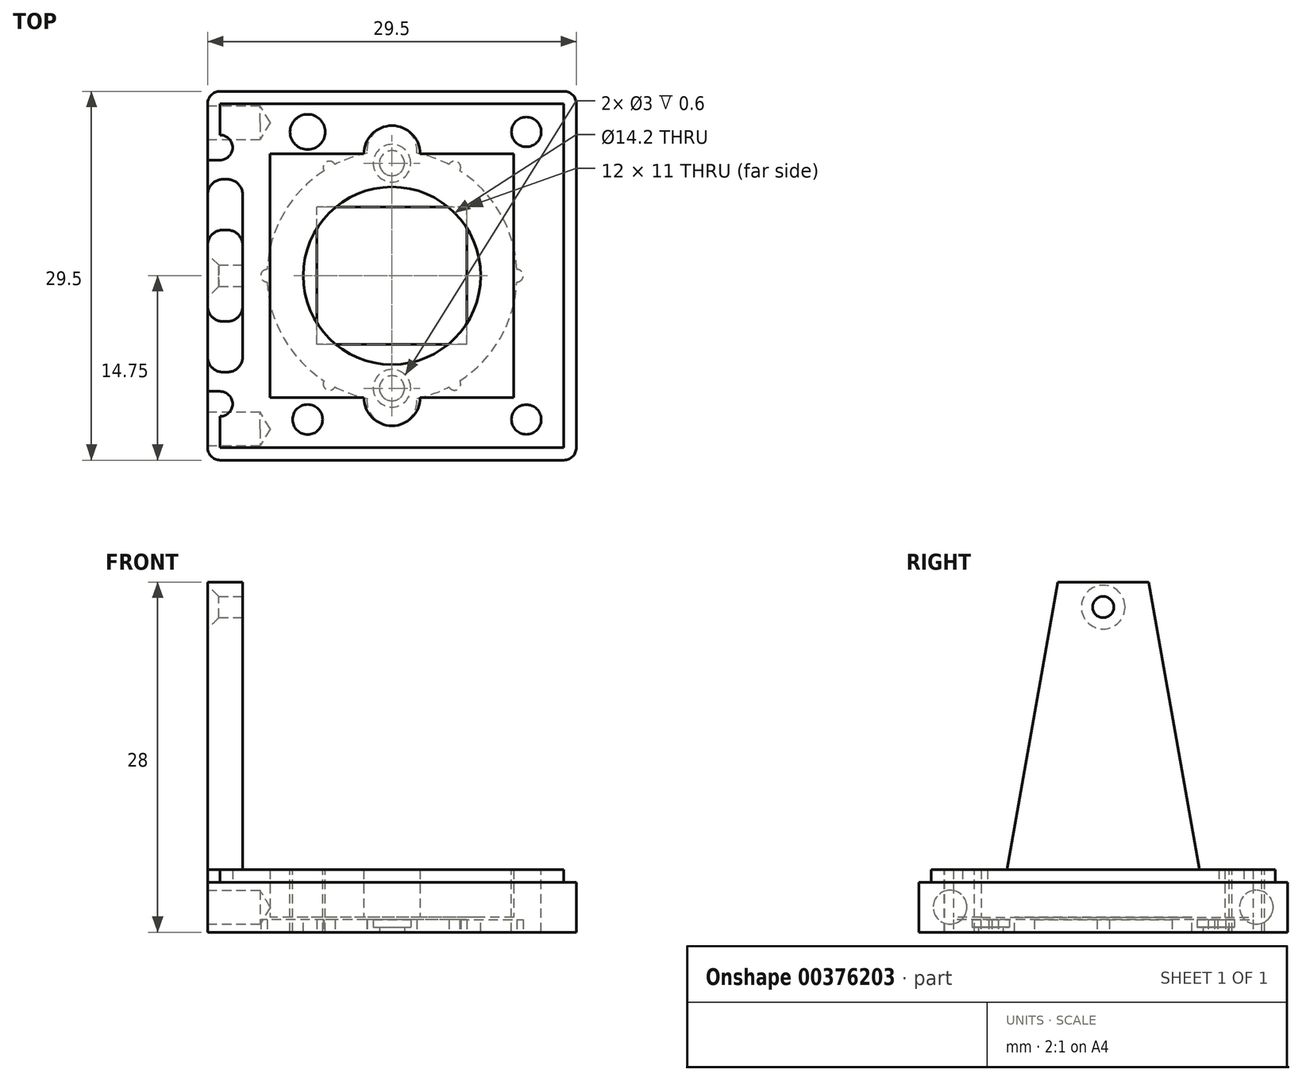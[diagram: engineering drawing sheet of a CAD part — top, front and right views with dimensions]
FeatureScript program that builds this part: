
annotation { "Feature Type Name" : "Feature", "Feature Type Description" : "" }
export const myFeature = defineFeature(function(context is Context, id is Id, definition is map)
    precondition{}
    {
        {
            var Q0;
            Q0=qCreatedBy(makeId("Top.planeOp"),FACE);
            var sketch = newSketch(context, id + "F0", { "sketchPlane" : qUnion([Q0])});
            skLineSegment(sketch, "E0.bottom", {"start": v(14.75, -14.75) * mm, "end": v(-14.75, -14.75) * mm});
            skLineSegment(sketch, "E0.top", {"start": v(14.75, 14.75) * mm, "end": v(-14.75, 14.75) * mm});
            skLineSegment(sketch, "E0.left", {"start": v(14.75, -14.75) * mm, "end": v(14.75, 14.75) * mm});
            skLineSegment(sketch, "E0.right", {"start": v(-14.75, -14.75) * mm, "end": v(-14.75, 14.75) * mm});
            skPoint(sketch, "E0.middle", {"position": v(0, 0) * mm});
            skLineSegment(sketch, "E1.0", {"start": v(-9.75, -9.75) * mm, "end": v(-9.75, 9.75) * mm});
            skLineSegment(sketch, "E1.1", {"start": v(9.75, -9.75) * mm, "end": v(-9.75, -9.75) * mm});
            skLineSegment(sketch, "E1.2", {"start": v(9.75, -9.75) * mm, "end": v(9.75, 9.75) * mm});
            skLineSegment(sketch, "E1.3", {"start": v(9.75, 9.75) * mm, "end": v(-9.75, 9.75) * mm});
            skSolve(sketch);
        }
        {
            var Q0;
            Q0=qSketchRegion(id+"F0",true);
            extrude(context, id + "F1", {"entities" : qUnion([Q0]), "depth" : 4 * mm, "offsetDistance" : 25 * mm});
        }
        {
            var Q0;
            Q0=makeQuery(id+"F1.opExtrude","CAP_FACE",FACE,{"disambiguationData":[OSD([sQuery(id+"F0.wireOp",EDGE,"E0.bottom"),sQuery(id+"F0.wireOp",EDGE,"E0.top"),sQuery(id+"F0.wireOp",EDGE,"E0.left"),sQuery(id+"F0.wireOp",EDGE,"E0.right"),sQuery(id+"F0.wireOp",EDGE,"E1.0"),sQuery(id+"F0.wireOp",EDGE,"E1.1"),sQuery(id+"F0.wireOp",EDGE,"E1.2"),sQuery(id+"F0.wireOp",EDGE,"E1.3")])],"isStart":false});
            var sketch = newSketch(context, id + "F2", { "sketchPlane" : qUnion([Q0])});
            skLineSegment(sketch, "E2.0", {"start": v(13.75, 13.75) * mm, "end": v(-13.75, 13.75) * mm});
            skLineSegment(sketch, "E2.1", {"start": v(13.75, -13.75) * mm, "end": v(13.75, 13.75) * mm});
            skLineSegment(sketch, "E2.2", {"start": v(13.75, -13.75) * mm, "end": v(-13.75, -13.75) * mm});
            skLineSegment(sketch, "E2.3", {"start": v(-13.75, -13.75) * mm, "end": v(-13.75, -11.25) * mm});
            skLineSegment(sketch, "E3.bottom", {"start": v(-14.75, -8.65) * mm, "end": v(-11.95, -8.65) * mm});
            skLineSegment(sketch, "E3.top", {"start": v(-14.75, 8.65) * mm, "end": v(-11.95, 8.65) * mm});
            skLineSegment(sketch, "E3.left", {"start": v(-14.75, -8.65) * mm, "end": v(-14.75, 8.65) * mm});
            skLineSegment(sketch, "E3.right", {"start": v(-11.95, -8.65) * mm, "end": v(-11.95, 8.65) * mm});
            skPoint(sketch, "E3.middle", {"position": v(-13.35, 0) * mm});
            skPoint(sketch, "E3.middle.positionSnap0", {"position": v(-13.75, 0) * mm});
            skPoint(sketch, "E3.centerSnap0", {"position": v(-13.75, 0) * mm});
            skLineSegment(sketch, "E4.trimOffspring", {"start": v(-13.75, 11.25) * mm, "end": v(-13.75, 13.75) * mm});
            skArc(sketch, "E5", {"start": v(-13.75, 9.25) * mm, "mid": v(-12.75, 10.25) * mm, "end": v(-13.75, 11.25) * mm});
            skArc(sketch, "E6", {"start": v(-13.75, -11.25) * mm, "mid": v(-12.75, -10.25) * mm, "end": v(-13.75, -9.25) * mm});
            skLineSegment(sketch, "E7", {"start": v(-13.75, -9.25) * mm, "end": v(-14.75, -9.25) * mm});
            skLineSegment(sketch, "E8", {"start": v(-13.75, 9.25) * mm, "end": v(-14.75, 9.25) * mm});
            skCircle(sketch, "E9", {"center": v(0, 9.75) * mm, "radius": 2.25 * mm});
            skCircle(sketch, "E10", {"center": v(0, -9.75) * mm, "radius": 2.25 * mm});
            skLineSegment(sketch, "E11", {"start": v(-13.35, 0) * mm, "end": v(0, 0) * mm, "construction": true});
            skLineSegment(sketch, "E12.bottom", {"start": v(6, -7) * mm, "end": v(-6, -7) * mm, "construction": true});
            skLineSegment(sketch, "E12.top", {"start": v(6, 7) * mm, "end": v(-6, 7) * mm, "construction": true});
            skLineSegment(sketch, "E12.left", {"start": v(6, -7) * mm, "end": v(6, 7) * mm, "construction": true});
            skLineSegment(sketch, "E12.right", {"start": v(-6, -7) * mm, "end": v(-6, 7) * mm, "construction": true});
            skPoint(sketch, "E12.middle", {"position": v(0, 0) * mm});
            skCircle(sketch, "E13", {"center": v(0, 0) * mm, "radius": 7.1 * mm});
            skSolve(sketch);
        }
        {
            var Q0;
            {var subQ5=sQuery(id+"F2.wireOp",EDGE,"E8");Q0=makeQuery(id+"F2.imprint","IMPRINT",FACE,{"disambiguationData":[TD([[makeQuery(id+"F2.imprint","IMPRINT",EDGE,{"derivedFrom":subQ5}),1.0]])]});}
            var Q1;
            {var subQ8=sQuery(id+"F2.wireOp",EDGE,"E2.0");Q1=makeQuery(id+"F2.imprint","IMPRINT",FACE,{"disambiguationData":[TD([[makeQuery(id+"F2.imprint","IMPRINT",EDGE,{"derivedFrom":subQ8}),1.0]])]});}
            var Q2;
            {var subQ3=sQuery(id+"F2.wireOp",EDGE,"E7");Q2=makeQuery(id+"F2.imprint","IMPRINT",FACE,{"disambiguationData":[TD([[makeQuery(id+"F2.imprint","IMPRINT",EDGE,{"derivedFrom":subQ3}),-1.0]])]});}
            var Q3;
            {var subQ3=sQuery(id+"F2.wireOp",EDGE,"E3.left");Q3=makeQuery(id+"F2.imprint","IMPRINT",FACE,{"disambiguationData":[TD([[makeQuery(id+"F2.imprint","IMPRINT",EDGE,{"derivedFrom":subQ3}),-1.0]])]});}
            var Q4;
            Q4=makeQuery(id+"F2.imprint","IMPRINT",FACE,{"disambiguationData":[TD([[makeQuery(id+"F2.imprint","IMPRINT",EDGE,{"derivedFrom":sQuery(id+"F2.wireOp",EDGE,"E12.bottom")}),1.0]])]});
            var Q5;
            {var subQ0=sQuery(id+"F2.wireOp",EDGE,"E9");var subQ1=makeQuery(id+"F1.opExtrude","CAP_EDGE",EDGE,{"disambiguationData":[OSD([sQuery(id+"F0.wireOp",EDGE,"E1.3")])],"isStart":false});var subQ2=makeQuery(id+"F2.imprint","INTERSECT",VERTEX,{"disambiguationData":[OD(0.0)],"derivedFrom":[subQ1,subQ0]});Q5=makeQuery(id+"F2.imprint","IMPRINT",FACE,{"disambiguationData":[TD([[makeQuery(id+"F2.imprint","IMPRINT",EDGE,{"disambiguationData":[TD([[subQ2,-1.0]])],"derivedFrom":subQ0}),1.0]])]});}
            var Q6;
            {var subQ0=sQuery(id+"F2.wireOp",EDGE,"E9");var subQ1=makeQuery(id+"F1.opExtrude","CAP_EDGE",EDGE,{"disambiguationData":[OSD([sQuery(id+"F0.wireOp",EDGE,"E1.3")])],"isStart":false});var subQ2=makeQuery(id+"F2.imprint","INTERSECT",VERTEX,{"disambiguationData":[OD(0.0)],"derivedFrom":[subQ1,subQ0]});Q6=makeQuery(id+"F2.imprint","IMPRINT",FACE,{"disambiguationData":[TD([[makeQuery(id+"F2.imprint","IMPRINT",EDGE,{"disambiguationData":[TD([[subQ2,1.0]])],"derivedFrom":subQ0}),1.0]])]});}
            var Q7;
            {var subQ0=sQuery(id+"F2.wireOp",EDGE,"E10");var subQ1=makeQuery(id+"F1.opExtrude","CAP_EDGE",EDGE,{"disambiguationData":[OSD([sQuery(id+"F0.wireOp",EDGE,"E1.1")])],"isStart":false});var subQ2=makeQuery(id+"F2.imprint","INTERSECT",VERTEX,{"disambiguationData":[OD(0.0)],"derivedFrom":[subQ1,subQ0]});Q7=makeQuery(id+"F2.imprint","IMPRINT",FACE,{"disambiguationData":[TD([[makeQuery(id+"F2.imprint","IMPRINT",EDGE,{"disambiguationData":[TD([[subQ2,-1.0]])],"derivedFrom":subQ0}),1.0]])]});}
            var Q8;
            {var subQ0=sQuery(id+"F2.wireOp",EDGE,"E10");var subQ1=makeQuery(id+"F1.opExtrude","CAP_EDGE",EDGE,{"disambiguationData":[OSD([sQuery(id+"F0.wireOp",EDGE,"E1.1")])],"isStart":false});var subQ2=makeQuery(id+"F2.imprint","INTERSECT",VERTEX,{"disambiguationData":[OD(0.0)],"derivedFrom":[subQ1,subQ0]});Q8=makeQuery(id+"F2.imprint","IMPRINT",FACE,{"disambiguationData":[TD([[makeQuery(id+"F2.imprint","IMPRINT",EDGE,{"disambiguationData":[TD([[subQ2,1.0]])],"derivedFrom":subQ0}),1.0]])]});}
            var Q9;
            {var subQ0=sQuery(id+"F2.wireOp",EDGE,"wOXAMDxP-vdY0-njxj-25cC-4RGBukaj3HmT");var subQ1=makeQuery(id+"F1.opExtrude","CAP_EDGE",EDGE,{"disambiguationData":[OSD([sQuery(id+"F0.wireOp",EDGE,"E1.1")])],"isStart":false});var subQ2=makeQuery(id+"F2.imprint","INTERSECT",VERTEX,{"disambiguationData":[OD(0.0)],"derivedFrom":[subQ1,subQ0]});Q9=makeQuery(id+"F2.imprint","IMPRINT",FACE,{"disambiguationData":[TD([[makeQuery(id+"F2.imprint","IMPRINT",EDGE,{"disambiguationData":[TD([[subQ2,-1.0]])],"derivedFrom":subQ0}),1.0]])]});}
            var Q10;
            {var subQ0=sQuery(id+"F2.wireOp",EDGE,"dd9HisNv-PFn9-XoiM-mcjF-Oo7U2ipqZEaN");var subQ1=makeQuery(id+"F1.opExtrude","CAP_EDGE",EDGE,{"disambiguationData":[OSD([sQuery(id+"F0.wireOp",EDGE,"E1.3")])],"isStart":false});var subQ2=makeQuery(id+"F2.imprint","INTERSECT",VERTEX,{"disambiguationData":[OD(0.0)],"derivedFrom":[subQ1,subQ0]});Q10=makeQuery(id+"F2.imprint","IMPRINT",FACE,{"disambiguationData":[TD([[makeQuery(id+"F2.imprint","IMPRINT",EDGE,{"disambiguationData":[TD([[subQ2,-1.0]])],"derivedFrom":subQ0}),1.0]])]});}
            var Q11;
            {var subQ0=sQuery(id+"F2.wireOp",EDGE,"dd9HisNv-PFn9-XoiM-mcjF-Oo7U2ipqZEaN");var subQ1=makeQuery(id+"F1.opExtrude","CAP_EDGE",EDGE,{"disambiguationData":[OSD([sQuery(id+"F0.wireOp",EDGE,"E1.3")])],"isStart":false});var subQ2=makeQuery(id+"F2.imprint","INTERSECT",VERTEX,{"disambiguationData":[OD(0.0)],"derivedFrom":[subQ1,subQ0]});Q11=makeQuery(id+"F2.imprint","IMPRINT",FACE,{"disambiguationData":[TD([[makeQuery(id+"F2.imprint","IMPRINT",EDGE,{"disambiguationData":[TD([[subQ2,1.0]])],"derivedFrom":subQ0}),1.0]])]});}
            var Q12;
            {var subQ0=sQuery(id+"F2.wireOp",EDGE,"wOXAMDxP-vdY0-njxj-25cC-4RGBukaj3HmT");var subQ1=makeQuery(id+"F1.opExtrude","CAP_EDGE",EDGE,{"disambiguationData":[OSD([sQuery(id+"F0.wireOp",EDGE,"E1.1")])],"isStart":false});var subQ2=makeQuery(id+"F2.imprint","INTERSECT",VERTEX,{"disambiguationData":[OD(0.0)],"derivedFrom":[subQ1,subQ0]});Q12=makeQuery(id+"F2.imprint","IMPRINT",FACE,{"disambiguationData":[TD([[makeQuery(id+"F2.imprint","IMPRINT",EDGE,{"disambiguationData":[TD([[subQ2,1.0]])],"derivedFrom":subQ0}),1.0]])]});}
            var Q13;
            Q13=makeQuery(id+"F2.imprint","IMPRINT",FACE,{"disambiguationData":[TD([[makeQuery(id+"F2.imprint","IMPRINT",EDGE,{"derivedFrom":sQuery(id+"F2.wireOp",EDGE,"E13")}),-1.0]])]});
            extrude(context, id + "F3", {"entities" : qUnion([Q0, Q1, Q2, Q3, Q4, Q5, Q6, Q7, Q8, Q9, Q10, Q11, Q12, Q13]), "operationType" : NewBodyOperationType.ADD, "oppositeDirection" : true, "depth" : 4 * mm, "offsetDistance" : 25 * mm, "hasSecondDirection" : true, "secondDirectionOppositeDirection" : true, "secondDirectionDepth" : 2.6 * mm});
        }
        {
            var Q0;
            Q0=makeQuery(id+"F2.imprint","IMPRINT",FACE,{"disambiguationData":[TD([[makeQuery(id+"F2.imprint","IMPRINT",EDGE,{"derivedFrom":sQuery(id+"F2.wireOp",EDGE,"E2.0")}),1.0]])]});
            var Q1;
            Q1=makeQuery(id+"F2.imprint","IMPRINT",FACE,{"disambiguationData":[TD([[makeQuery(id+"F2.imprint","IMPRINT",EDGE,{"derivedFrom":sQuery(id+"F2.wireOp",EDGE,"E3.bottom")}),1.0]])]});
            extrude(context, id + "F4", {"entities" : qUnion([Q0, Q1]), "operationType" : NewBodyOperationType.ADD, "depth" : 1 * mm, "offsetDistance" : 25 * mm});
        }
        {
            var Q0;
            {var subQ5=sQuery(id+"F2.wireOp",EDGE,"E3.left");Q0=makeQuery(id+"F2.imprint","IMPRINT",FACE,{"disambiguationData":[TD([[makeQuery(id+"F2.imprint","IMPRINT",EDGE,{"derivedFrom":subQ5}),-1.0]])]});}
            var Q1;
            {var subQ5=sQuery(id+"F2.wireOp",EDGE,"E3.right");Q1=makeQuery(id+"F2.imprint","IMPRINT",FACE,{"disambiguationData":[TD([[makeQuery(id+"F2.imprint","IMPRINT",EDGE,{"derivedFrom":subQ5}),1.0]])]});}
            extrude(context, id + "F5", {"entities" : qUnion([Q0, Q1]), "operationType" : NewBodyOperationType.ADD, "depth" : 24 * mm, "offsetDistance" : 25 * mm});
        }
        {
            var Q0;
            Q0=makeQuery(id+"F5.opExtrude","CAP_EDGE",EDGE,{"disambiguationData":[OSD([sQuery(id+"F2.wireOp",EDGE,"E3.bottom")])],"isStart":false});
            var Q1;
            Q1=makeQuery(id+"F5.opExtrude","CAP_EDGE",EDGE,{"disambiguationData":[OSD([sQuery(id+"F2.wireOp",EDGE,"E3.top")])],"isStart":false});
            chamfer(context, id + "F6", {"entities" : qUnion([Q0, Q1]), "chamferType" : ChamferType.OFFSET_ANGLE, "width" : 5 * mm, "oppositeDirection" : false, "angle" : 80 * degree, "tangentPropagation" : true});
        }
        {
            var Q0;
            Q0=makeQuery(id+"F6.opChamfer","BLEND_EDGE",EDGE,{"blendedFrom":[makeQuery(id+"F5.opExtrude","CAP_EDGE",EDGE,{"disambiguationData":[OSD([sQuery(id+"F2.wireOp",EDGE,"E3.bottom")])],"isStart":false}),makeQuery(id+"F5.opExtrude","SWEPT_FACE",FACE,{"disambiguationData":[OSD([sQuery(id+"F2.wireOp",EDGE,"E3.right")])]})],"blendedInto":[makeQuery(id+"F5.opExtrude","SWEPT_FACE",FACE,{"disambiguationData":[OSD([sQuery(id+"F2.wireOp",EDGE,"E3.right")])]})]});
            var Q1;
            Q1=makeQuery(id+"F6.opChamfer","BLEND_EDGE",EDGE,{"blendedFrom":[makeQuery(id+"F5.opExtrude","CAP_EDGE",EDGE,{"disambiguationData":[OSD([sQuery(id+"F2.wireOp",EDGE,"E3.bottom")])],"isStart":false}),makeQuery(id+"F5.boolean.opBoolean","MERGE",FACE,{"derivedFrom":[makeQuery(id+"F1.opExtrude","SWEPT_FACE",FACE,{"disambiguationData":[OSD([sQuery(id+"F0.wireOp",EDGE,"E0.right")])]}),makeQuery(id+"F5.opExtrude","SWEPT_FACE",FACE,{"disambiguationData":[OSD([sQuery(id+"F2.wireOp",EDGE,"E3.left")])]})]})],"blendedInto":[makeQuery(id+"F5.boolean.opBoolean","MERGE",FACE,{"derivedFrom":[makeQuery(id+"F1.opExtrude","SWEPT_FACE",FACE,{"disambiguationData":[OSD([sQuery(id+"F0.wireOp",EDGE,"E0.right")])]}),makeQuery(id+"F5.opExtrude","SWEPT_FACE",FACE,{"disambiguationData":[OSD([sQuery(id+"F2.wireOp",EDGE,"E3.left")])]})]})]});
            var Q2;
            Q2=makeQuery(id+"F6.opChamfer","BLEND_EDGE",EDGE,{"blendedFrom":[makeQuery(id+"F5.opExtrude","CAP_EDGE",EDGE,{"disambiguationData":[OSD([sQuery(id+"F2.wireOp",EDGE,"E3.top")])],"isStart":false}),makeQuery(id+"F5.opExtrude","SWEPT_FACE",FACE,{"disambiguationData":[OSD([sQuery(id+"F2.wireOp",EDGE,"E3.right")])]})],"blendedInto":[makeQuery(id+"F5.opExtrude","SWEPT_FACE",FACE,{"disambiguationData":[OSD([sQuery(id+"F2.wireOp",EDGE,"E3.right")])]})]});
            var Q3;
            Q3=makeQuery(id+"F6.opChamfer","BLEND_EDGE",EDGE,{"blendedFrom":[makeQuery(id+"F5.opExtrude","CAP_EDGE",EDGE,{"disambiguationData":[OSD([sQuery(id+"F2.wireOp",EDGE,"E3.top")])],"isStart":false}),makeQuery(id+"F5.boolean.opBoolean","MERGE",FACE,{"derivedFrom":[makeQuery(id+"F1.opExtrude","SWEPT_FACE",FACE,{"disambiguationData":[OSD([sQuery(id+"F0.wireOp",EDGE,"E0.right")])]}),makeQuery(id+"F5.opExtrude","SWEPT_FACE",FACE,{"disambiguationData":[OSD([sQuery(id+"F2.wireOp",EDGE,"E3.left")])]})]})],"blendedInto":[makeQuery(id+"F5.boolean.opBoolean","MERGE",FACE,{"derivedFrom":[makeQuery(id+"F1.opExtrude","SWEPT_FACE",FACE,{"disambiguationData":[OSD([sQuery(id+"F0.wireOp",EDGE,"E0.right")])]}),makeQuery(id+"F5.opExtrude","SWEPT_FACE",FACE,{"disambiguationData":[OSD([sQuery(id+"F2.wireOp",EDGE,"E3.left")])]})]})]});
            fillet(context, id + "F7", {"entities" : qUnion([Q0, Q1, Q2, Q3]), "radius" : 1.2 * mm, "tangentPropagation" : true, "allowEdgeOverflow" : false});
        }
        {
            var Q0;
            Q0=makeQuery(id+"F4.opExtrude","CAP_FACE",FACE,{"disambiguationData":[OSD([sQuery(id+"F0.wireOp",EDGE,"E0.right"),sQuery(id+"F0.wireOp",EDGE,"E1.0"),sQuery(id+"F0.wireOp",EDGE,"E1.1"),sQuery(id+"F0.wireOp",EDGE,"E1.2"),sQuery(id+"F0.wireOp",EDGE,"E1.3"),sQuery(id+"F2.wireOp",EDGE,"E2.0"),sQuery(id+"F2.wireOp",EDGE,"E2.1"),sQuery(id+"F2.wireOp",EDGE,"E2.2"),sQuery(id+"F2.wireOp",EDGE,"E2.3"),sQuery(id+"F2.wireOp",EDGE,"E3.left"),sQuery(id+"F2.wireOp",EDGE,"E4.trimOffspring"),sQuery(id+"F2.wireOp",EDGE,"E5"),sQuery(id+"F2.wireOp",EDGE,"E6"),sQuery(id+"F2.wireOp",EDGE,"E7"),sQuery(id+"F2.wireOp",EDGE,"E8"),sQuery(id+"F2.wireOp",EDGE,"E9"),sQuery(id+"F2.wireOp",EDGE,"E10")])],"isStart":false});
            var sketch = newSketch(context, id + "F8", { "sketchPlane" : qUnion([Q0])});
            skCircle(sketch, "E14", {"center": v(10.75, 11.5) * mm, "radius": 1.19 * mm});
            skCircle(sketch, "E15", {"center": v(10.75, -11.5) * mm, "radius": 1.19 * mm});
            skCircle(sketch, "E16", {"center": v(-6.75, 11.5) * mm, "radius": 1.4 * mm});
            skCircle(sketch, "E17", {"center": v(-6.75, -11.5) * mm, "radius": 1.2 * mm});
            skLineSegment(sketch, "E18", {"start": v(0, 0) * mm, "end": v(6.78, 0) * mm, "construction": true});
            skSolve(sketch);
        }
        {
            var Q0;
            Q0=sQuery(id+"F8.wireOp",VERTEX,"E14.center");
            var Q1;
            Q1=sQuery(id+"F8.wireOp",VERTEX,"E15.center");
            var Q2;
            Q2=sQuery(id+"F8.wireOp",VERTEX,"E16.center");
            var Q3;
            Q3=sQuery(id+"F8.wireOp",VERTEX,"E17.center");
            var Q4;
            Q4=makeQuery(id+"F1.opExtrude","SWEPT_BODY",BODY,{"disambiguationData":[OSD([sQuery(id+"F0.wireOp",EDGE,"E0.bottom"),sQuery(id+"F0.wireOp",EDGE,"E0.top"),sQuery(id+"F0.wireOp",EDGE,"E0.left"),sQuery(id+"F0.wireOp",EDGE,"E0.right"),sQuery(id+"F0.wireOp",EDGE,"E1.0"),sQuery(id+"F0.wireOp",EDGE,"E1.1"),sQuery(id+"F0.wireOp",EDGE,"E1.2"),sQuery(id+"F0.wireOp",EDGE,"E1.3")])]});
            hole(context, id + "F9", {"style" : HoleStyle.SIMPLE, "endStyle" : HoleEndStyle.BLIND, "holeDiameter" : 2.2 * mm, "majorDiameter" : 5 * mm, "holeDepth" : 20 * mm, "isTappedThrough" : true, "tappedDepth" : 12 * mm, "tapClearance" : 3, "locations" : qUnion([Q0, Q1, Q2, Q3]), "scope" : qUnion([Q4])});
        }
        {
            var Q0;
            Q0=qCreatedBy(makeId("Top.planeOp"),FACE);
            var sketch = newSketch(context, id + "F10", { "sketchPlane" : qUnion([Q0])});
            skCircle(sketch, "E19", {"center": v(0, 0) * mm, "radius": 10 * mm});
            skLineSegment(sketch, "E20.bottom", {"start": v(6, -5.5) * mm, "end": v(-6, -5.5) * mm});
            skLineSegment(sketch, "E20.top", {"start": v(6, 5.5) * mm, "end": v(-6, 5.5) * mm});
            skLineSegment(sketch, "E20.left", {"start": v(6, -5.5) * mm, "end": v(6, 5.5) * mm});
            skLineSegment(sketch, "E20.right", {"start": v(-6, -5.5) * mm, "end": v(-6, 5.5) * mm});
            skCircle(sketch, "E21", {"center": v(0, 10) * mm, "radius": 2 * mm});
            skCircle(sketch, "E22", {"center": v(0, -10) * mm, "radius": 2 * mm});
            skCircle(sketch, "E23", {"center": v(10, 0) * mm, "radius": 0.5 * mm});
            skCircle(sketch, "E24.1.0", {"center": v(5, 8.66) * mm, "radius": 0.5 * mm});
            skCircle(sketch, "E24.2.0", {"center": v(-5, 8.66) * mm, "radius": 0.5 * mm});
            skCircle(sketch, "E25.1.3.0", {"center": v(-10, 0) * mm, "radius": 0.5 * mm});
            skCircle(sketch, "E25.1.4.0", {"center": v(-5, -8.66) * mm, "radius": 0.5 * mm});
            skCircle(sketch, "E25.1.5.0", {"center": v(5, -8.66) * mm, "radius": 0.5 * mm});
            skSolve(sketch);
        }
        {
            var Q0;
            Q0=qSketchRegion(id+"F10",true);
            var Q1;
            {var subQ0=sQuery(id+"F10.wireOp",EDGE,"nrrdsNW8-0lje-5FPb-w1w5-OaGebltPMd51");var subQ1=sQuery(id+"F10.wireOp",EDGE,"E19");var subQ2=makeQuery(id+"F10.imprint","INTERSECT",VERTEX,{"disambiguationData":[OD(0.0)],"derivedFrom":[subQ1,subQ0]});Q1=makeQuery(id+"F10.imprint","IMPRINT",FACE,{"disambiguationData":[TD([[makeQuery(id+"F10.imprint","IMPRINT",EDGE,{"disambiguationData":[TD([[subQ2,-1.0]])],"derivedFrom":subQ1}),1.0]])]});}
            var Q2;
            {var subQ0=sQuery(id+"F10.wireOp",EDGE,"nrrdsNW8-0lje-5FPb-w1w5-OaGebltPMd51");var subQ1=sQuery(id+"F10.wireOp",EDGE,"E19");var subQ2=makeQuery(id+"F10.imprint","INTERSECT",VERTEX,{"disambiguationData":[OD(0.0)],"derivedFrom":[subQ1,subQ0]});Q2=makeQuery(id+"F10.imprint","IMPRINT",FACE,{"disambiguationData":[TD([[makeQuery(id+"F10.imprint","IMPRINT",EDGE,{"disambiguationData":[TD([[subQ2,-1.0]])],"derivedFrom":subQ1}),-1.0]])]});}
            var Q3;
            {var subQ0=sQuery(id+"F10.wireOp",EDGE,"nrrdsNW8-0lje-5FPb-w1w5-OaGebltPMd51");var subQ1=sQuery(id+"F10.wireOp",EDGE,"E21");var subQ2=makeQuery(id+"F10.imprint","INTERSECT",VERTEX,{"disambiguationData":[OD(0.0)],"derivedFrom":[subQ1,subQ0]});Q3=makeQuery(id+"F10.imprint","IMPRINT",FACE,{"disambiguationData":[TD([[makeQuery(id+"F10.imprint","IMPRINT",EDGE,{"disambiguationData":[TD([[subQ2,-1.0]])],"derivedFrom":subQ1}),-1.0]])]});}
            var Q4;
            {var subQ0=sQuery(id+"F10.wireOp",EDGE,"S1DDepDF-IZdj-yKmF-IfUE-yXN7PUjpcanx");var subQ1=sQuery(id+"F10.wireOp",EDGE,"E19");var subQ2=makeQuery(id+"F10.imprint","INTERSECT",VERTEX,{"disambiguationData":[OD(0.0)],"derivedFrom":[subQ1,subQ0]});Q4=makeQuery(id+"F10.imprint","IMPRINT",FACE,{"disambiguationData":[TD([[makeQuery(id+"F10.imprint","IMPRINT",EDGE,{"disambiguationData":[TD([[subQ2,-1.0]])],"derivedFrom":subQ1}),1.0]])]});}
            var Q5;
            {var subQ0=sQuery(id+"F10.wireOp",EDGE,"S1DDepDF-IZdj-yKmF-IfUE-yXN7PUjpcanx");var subQ1=sQuery(id+"F10.wireOp",EDGE,"E22");var subQ2=makeQuery(id+"F10.imprint","INTERSECT",VERTEX,{"disambiguationData":[OD(0.0)],"derivedFrom":[subQ1,subQ0]});Q5=makeQuery(id+"F10.imprint","IMPRINT",FACE,{"disambiguationData":[TD([[makeQuery(id+"F10.imprint","IMPRINT",EDGE,{"disambiguationData":[TD([[subQ2,-1.0]])],"derivedFrom":subQ1}),-1.0]])]});}
            var Q6;
            {var subQ0=sQuery(id+"F10.wireOp",EDGE,"S1DDepDF-IZdj-yKmF-IfUE-yXN7PUjpcanx");var subQ1=sQuery(id+"F10.wireOp",EDGE,"E19");var subQ2=makeQuery(id+"F10.imprint","INTERSECT",VERTEX,{"disambiguationData":[OD(0.0)],"derivedFrom":[subQ1,subQ0]});Q6=makeQuery(id+"F10.imprint","IMPRINT",FACE,{"disambiguationData":[TD([[makeQuery(id+"F10.imprint","IMPRINT",EDGE,{"disambiguationData":[TD([[subQ2,-1.0]])],"derivedFrom":subQ1}),-1.0]])]});}
            extrude(context, id + "F11", {"entities" : qUnion([Q0, Q1, Q2, Q3, Q4, Q5, Q6]), "depth" : 1 * mm, "offsetDistance" : 25 * mm});
        }
        {
            var Q0;
            {var subQ0=sQuery(id+"F2.wireOp",EDGE,"E3.left");var subQ1=sQuery(id+"F0.wireOp",EDGE,"E0.right");Q0=makeQuery(id+"F5.boolean.opBoolean","MERGE",FACE,{"derivedFrom":[makeQuery(id+"F4.boolean.opBoolean","MERGE",FACE,{"derivedFrom":[makeQuery(id+"F1.opExtrude","SWEPT_FACE",FACE,{"disambiguationData":[OSD([subQ1])]}),makeQuery(id+"F4.opExtrude","SWEPT_FACE",FACE,{"disambiguationData":[OSD([subQ1,subQ0])]})]}),makeQuery(id+"F5.opExtrude","SWEPT_FACE",FACE,{"disambiguationData":[OSD([subQ0])]})]});}
            var sketch = newSketch(context, id + "F12", { "sketchPlane" : qUnion([Q0])});
            skCircle(sketch, "E26", {"center": v(0, 26) * mm, "radius": 0.1 * mm});
            skCircle(sketch, "E27", {"center": v(-12.25, 2) * mm, "radius": 1.3 * mm});
            skCircle(sketch, "E28", {"center": v(12.25, 2) * mm, "radius": 1.3 * mm});
            skPoint(sketch, "E29.endSnap0", {"position": v(14.75, 2) * mm});
            skLineSegment(sketch, "E30", {"start": v(14.75, 2) * mm, "end": v(-14.75, 2) * mm, "construction": true});
            skSolve(sketch);
        }
        {
            var Q0;
            Q0=sQuery(id+"F12.wireOp",VERTEX,"E26.center");
            var Q1;
            Q1=makeQuery(id+"F1.opExtrude","SWEPT_BODY",BODY,{"disambiguationData":[OSD([sQuery(id+"F0.wireOp",EDGE,"E0.bottom"),sQuery(id+"F0.wireOp",EDGE,"E0.top"),sQuery(id+"F0.wireOp",EDGE,"E0.left"),sQuery(id+"F0.wireOp",EDGE,"E0.right"),sQuery(id+"F0.wireOp",EDGE,"E1.0"),sQuery(id+"F0.wireOp",EDGE,"E1.1"),sQuery(id+"F0.wireOp",EDGE,"E1.2"),sQuery(id+"F0.wireOp",EDGE,"E1.3")])]});
            hole(context, id + "F13", {"style" : HoleStyle.C_SINK, "endStyle" : HoleEndStyle.BLIND, "holeDiameter" : 1.7 * mm, "cSinkDiameter" : 3.5 * mm, "cSinkAngle" : 90 * degree, "majorDiameter" : 5 * mm, "holeDepth" : 5 * mm, "isTappedThrough" : true, "tappedDepth" : 12 * mm, "tapClearance" : 3, "locations" : qUnion([Q0]), "scope" : qUnion([Q1])});
        }
        {
            var Q0;
            Q0=sQuery(id+"F12.wireOp",VERTEX,"E27.center");
            var Q1;
            Q1=sQuery(id+"F12.wireOp",VERTEX,"E28.center");
            var Q2;
            Q2=makeQuery(id+"F1.opExtrude","SWEPT_BODY",BODY,{"disambiguationData":[OSD([sQuery(id+"F0.wireOp",EDGE,"E0.bottom"),sQuery(id+"F0.wireOp",EDGE,"E0.top"),sQuery(id+"F0.wireOp",EDGE,"E0.left"),sQuery(id+"F0.wireOp",EDGE,"E0.right"),sQuery(id+"F0.wireOp",EDGE,"E1.0"),sQuery(id+"F0.wireOp",EDGE,"E1.1"),sQuery(id+"F0.wireOp",EDGE,"E1.2"),sQuery(id+"F0.wireOp",EDGE,"E1.3")])]});
            hole(context, id + "F14", {"style" : HoleStyle.SIMPLE, "endStyle" : HoleEndStyle.BLIND, "holeDiameter" : 2.7 * mm, "majorDiameter" : 5 * mm, "holeDepth" : 4.2 * mm, "isTappedThrough" : true, "tappedDepth" : 12 * mm, "tapClearance" : 3, "locations" : qUnion([Q0, Q1]), "scope" : qUnion([Q2])});
        }
        {
            var Q0;
            Q0=makeQuery(id+"F11.opExtrude","CAP_FACE",FACE,{"disambiguationData":[OSD([sQuery(id+"F10.wireOp",EDGE,"E19"),sQuery(id+"F10.wireOp",EDGE,"E20.bottom"),sQuery(id+"F10.wireOp",EDGE,"E20.top"),sQuery(id+"F10.wireOp",EDGE,"E20.left"),sQuery(id+"F10.wireOp",EDGE,"E20.right"),sQuery(id+"F10.wireOp",EDGE,"E21"),sQuery(id+"F10.wireOp",EDGE,"E22"),sQuery(id+"F10.wireOp",EDGE,"E23"),sQuery(id+"F10.wireOp",EDGE,"E24.1.0"),sQuery(id+"F10.wireOp",EDGE,"E24.2.0"),sQuery(id+"F10.wireOp",EDGE,"E25.1.3.0"),sQuery(id+"F10.wireOp",EDGE,"E25.1.4.0"),sQuery(id+"F10.wireOp",EDGE,"E25.1.5.0")])],"isStart":false});
            var sketch = newSketch(context, id + "F15", { "sketchPlane" : qUnion([Q0])});
            skCircle(sketch, "E31", {"center": v(0, 9) * mm, "radius": 0.98 * mm});
            skCircle(sketch, "E32", {"center": v(0, -9) * mm, "radius": 1.12 * mm});
            skSolve(sketch);
        }
        {
            var Q0;
            Q0=sQuery(id+"F15.wireOp",VERTEX,"E31.center");
            var Q1;
            Q1=sQuery(id+"F15.wireOp",VERTEX,"E32.center");
            var Q2;
            Q2=makeQuery(id+"F11.opExtrude","SWEPT_BODY",BODY,{"disambiguationData":[OSD([sQuery(id+"F10.wireOp",EDGE,"E19"),sQuery(id+"F10.wireOp",EDGE,"E20.bottom"),sQuery(id+"F10.wireOp",EDGE,"E20.top"),sQuery(id+"F10.wireOp",EDGE,"E20.left"),sQuery(id+"F10.wireOp",EDGE,"E20.right"),sQuery(id+"F10.wireOp",EDGE,"E21"),sQuery(id+"F10.wireOp",EDGE,"E22"),sQuery(id+"F10.wireOp",EDGE,"E23"),sQuery(id+"F10.wireOp",EDGE,"E24.1.0"),sQuery(id+"F10.wireOp",EDGE,"E24.2.0"),sQuery(id+"F10.wireOp",EDGE,"E25.1.3.0"),sQuery(id+"F10.wireOp",EDGE,"E25.1.4.0"),sQuery(id+"F10.wireOp",EDGE,"E25.1.5.0")])]});
            hole(context, id + "F16", {"style" : HoleStyle.C_BORE, "endStyle" : HoleEndStyle.BLIND, "holeDiameter" : 2 * mm, "cBoreDiameter" : 3 * mm, "cBoreDepth" : 0.6 * mm, "majorDiameter" : 5 * mm, "holeDepth" : 4.2 * mm, "isTappedThrough" : true, "tappedDepth" : 12 * mm, "tapClearance" : 3, "locations" : qUnion([Q0, Q1]), "scope" : qUnion([Q2])});
        }
        {
            var Q0;
            Q0 = qSketchRegion(id + "F8", true);
            extrude(context, id + "F17", {"entities" : qUnion([Q0]), "operationType" : NewBodyOperationType.REMOVE, "oppositeDirection" : true, "depth" : 25 * mm, "offsetDistance" : 25 * mm});
        }
        {
            var Q0;
            Q0=makeQuery(id+"F1.opExtrude","SWEPT_EDGE",EDGE,{"disambiguationData":[OSD([sQuery(id+"F0.wireOp",EDGE,"E0.bottom"),sQuery(id+"F0.wireOp",EDGE,"E0.right")])]});
            var Q1;
            Q1=makeQuery(id+"F3.opExtrude","SWEPT_EDGE",EDGE,{"disambiguationData":[OSD([sQuery(id+"F2.wireOp",EDGE,"E2.2"),sQuery(id+"F2.wireOp",EDGE,"E2.3")])]});
            var Q2;
            Q2=makeQuery(id+"F3.opExtrude","SWEPT_EDGE",EDGE,{"disambiguationData":[OSD([sQuery(id+"F2.wireOp",EDGE,"E2.1"),sQuery(id+"F2.wireOp",EDGE,"E2.2")])]});
            var Q3;
            Q3=makeQuery(id+"F1.opExtrude","SWEPT_EDGE",EDGE,{"disambiguationData":[OSD([sQuery(id+"F0.wireOp",EDGE,"E0.bottom"),sQuery(id+"F0.wireOp",EDGE,"E0.left")])]});
            var Q4;
            Q4=makeQuery(id+"F3.opExtrude","SWEPT_EDGE",EDGE,{"disambiguationData":[OSD([sQuery(id+"F2.wireOp",EDGE,"E2.0"),sQuery(id+"F2.wireOp",EDGE,"E2.1")])]});
            var Q5;
            Q5=makeQuery(id+"F1.opExtrude","SWEPT_EDGE",EDGE,{"disambiguationData":[OSD([sQuery(id+"F0.wireOp",EDGE,"E0.top"),sQuery(id+"F0.wireOp",EDGE,"E0.left")])]});
            var Q6;
            Q6=makeQuery(id+"F3.opExtrude","SWEPT_EDGE",EDGE,{"disambiguationData":[OSD([sQuery(id+"F2.wireOp",EDGE,"E2.0"),sQuery(id+"F2.wireOp",EDGE,"E4.trimOffspring")])]});
            var Q7;
            Q7=makeQuery(id+"F1.opExtrude","SWEPT_EDGE",EDGE,{"disambiguationData":[OSD([sQuery(id+"F0.wireOp",EDGE,"E0.top"),sQuery(id+"F0.wireOp",EDGE,"E0.right")])]});
            fillet(context, id + "F18", {"entities" : qUnion([Q0, Q1, Q2, Q3, Q4, Q5, Q6, Q7]), "radius" : 1 * mm, "tangentPropagation" : true, "allowEdgeOverflow" : false});
        }
        {
            var Q0;
            Q0=makeQuery(id+"F8.imprint","IMPRINT",FACE,{"disambiguationData":[TD([[makeQuery(id+"F8.imprint","IMPRINT",EDGE,{"derivedFrom":sQuery(id+"F8.wireOp",EDGE,"E14")}),-1.0]])]});
            var sketch = newSketch(context, id + "F19", { "sketchPlane" : qUnion([Q0])});
            skCircle(sketch, "E33", {"center": v(-7, -5) * mm, "radius": 0.5 * mm, "construction": true});
            skCircle(sketch, "E34", {"center": v(7, -5) * mm, "radius": 0.5 * mm, "construction": true});
            skCircle(sketch, "E35", {"center": v(7, 5) * mm, "radius": 0.5 * mm, "construction": true});
            skCircle(sketch, "E36", {"center": v(-7, 5) * mm, "radius": 0.5 * mm, "construction": true});
            skCircle(sketch, "E37", {"center": v(0, 9) * mm, "radius": 0.75 * mm});
            skCircle(sketch, "E38", {"center": v(0, -9) * mm, "radius": 0.75 * mm});
            skSolve(sketch);
        }
        {
            var Q0;
            Q0=qSketchRegion(id+"F19",true);
            var Q1;
            Q1=sQuery(id+"F19.wireOp",EDGE,"E33");
            var Q2;
            Q2=sQuery(id+"F19.wireOp",EDGE,"E34");
            var Q3;
            Q3=sQuery(id+"F19.wireOp",EDGE,"E35");
            var Q4;
            Q4=sQuery(id+"F19.wireOp",EDGE,"E36");
            extrude(context, id + "F20", {"entities" : qUnion([Q0]), "operationType" : NewBodyOperationType.ADD, "surfaceOperationType" : NewSurfaceOperationType.ADD, "surfaceEntities" : qUnion([Q1, Q2, Q3, Q4]), "oppositeDirection" : true, "depth" : 3.5 * mm, "offsetDistance" : 25 * mm, "hasSecondDirection" : true, "secondDirectionOppositeDirection" : true, "secondDirectionDepth" : 0.2 * mm});
        }
        {
            var Q0;
            {var subQ3=sQuery(id+"F2.wireOp",EDGE,"E9");Q0=makeQuery(id+"F8.imprint","IMPRINT",FACE,{"disambiguationData":[TD([[makeQuery(id+"F8.imprint","IMPRINT",EDGE,{"derivedFrom":makeQuery(id+"F4.opExtrude","CAP_EDGE",EDGE,{"disambiguationData":[OSD([subQ3])],"isStart":false})}),1.0]])]});}
            var Q1;
            Q1=sQuery(id+"F2.wireOp",EDGE,"E9");
            var Q2;
            Q2=sQuery(id+"F2.wireOp",EDGE,"E10");
            extrude(context, id + "F21", {"entities" : qUnion([Q0]), "operationType" : NewBodyOperationType.REMOVE, "surfaceEntities" : qUnion([Q1, Q2]), "oppositeDirection" : true, "depth" : 3.8 * mm, "offsetDistance" : 25 * mm});
        }
    });
